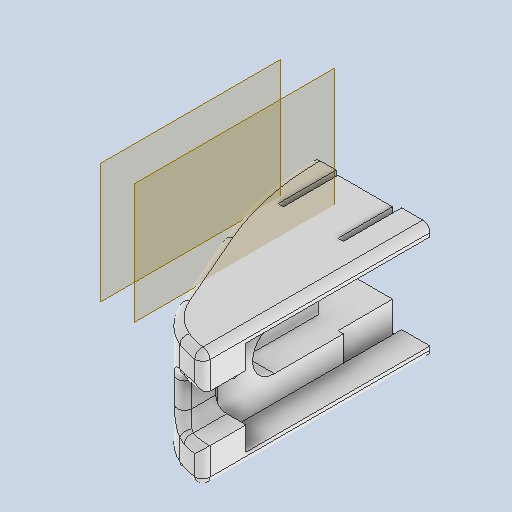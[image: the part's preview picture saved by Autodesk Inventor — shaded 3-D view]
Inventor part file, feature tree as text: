
AUTODESK INVENTOR PART (.ipt)
format: ipt  version: 2025 (Build 290162010, 162A)  size: 424,448 bytes
history: native  units: mm
features: extrude x8, sketch x7, other x4, hole x3, fillet x3, plane x2, reference x2, mirror x1
ambient origin geometry x8: Origin, YZ Plane, XZ Plane, XY Plane, X Axis, Y Axis, Z Axis, Center Point
bodies: Volumenkörper1 (feature_tree)
feature tree (30):
  sketch  "Skizze1"  dims[d0=5.0mm d1=45.0mm d2=30.0mm d3=0.0mm]
  extrude  "Extrusion1"  Depth=30.0mm TaperAngle=0.0deg
  hole  "Bohrung2"  [1 undecoded]
  extrude  "Extrusion2"  [1 undecoded]
  plane  "Arbeitsebene1"
  hole  "Bohrung4"  [1 undecoded]
  extrude  "Extrusion3"  Depth=2.0mm
  plane  "Arbeitsebene2"
  hole  "Bohrung5"  [1 undecoded]
  extrude  "Extrusion4"  Depth=2.0mm
  extrude  "Extrusion5"  Depth=2.0mm TaperAngle=0.0deg
  extrude  "Extrusion6"  [1 undecoded]
  fillet  "Rundung2"  Radius=7.8mm
  sketch  "Skizze13"  dims[d41=12.0mm d42=0.0mm d43=0.0mm d44=3.2mm d45=6.0mm d46=6.3mm d47=2.0mm d48=90.0deg d49=8.0mm d50=20.594885mm d51=12.0mm d52=8.0mm d53=0.0mm d54=-19.5mm d56=7.8mm d57=1.0mm d58=0.0mm d59=2.0mm d60=0.0mm d61=12.0mm d62=8.5mm d63=0.0mm d65=0.5mm d66=3.0mm d67=1.0mm d68=0.0mm d69=8.5mm d70=0.0mm d71=3.0mm d72=15.0mm d73=15.0mm d75=35.0mm d76=2.0mm d77=0.0mm d78=2.0mm]
  extrude  "Extrusion7"  Depth=2.0mm TaperAngle=0.0deg
  extrude  "Extrusion8"  Depth=2.0mm TaperAngle=0.0deg
  fillet  "Rundung3"  Radius=12.0mm
  mirror  "Spiegeln1"
  fillet  "Rundung4"  Radius=8.5mm
  reference  "Referenz1"
  sketch  "Skizze3"  dims[d4=15.0mm d14=6.5mm]
  reference  "Referenz3"
  sketch  "Skizze5"  dims[d15=5.0mm]
  sketch  "Skizze7"  dims[d16=1.567mm d17=8.0mm d18=4.0mm d19=2.0mm d20=90.0deg d21=10.0mm d22=20.594885mm d30=-10.0mm]
  sketch  "Skizze8"  dims[d31=15.0mm d32=15.0mm]
  sketch  "Skizze9"  dims[d33=3.2mm d34=6.0mm d35=6.3mm d36=2.0mm d37=90.0deg d38=8.0mm d39=20.594885mm d40=14.0mm]
  other  "<userpath>\GIT\HDVKBM\CAD\Krandemonstrator\Demonstrator.iam"
  other  "Demonstrator.iam"
  other  "Träger:1"
  other  "AS 1112 (2) - Metrisch M4  Typ 5:1"
note: 5 required parameter values undecoded (feature->parameter linkage not recoverable at this tier; creation-order binding heuristic only, values carry confidence <= 0.55)
